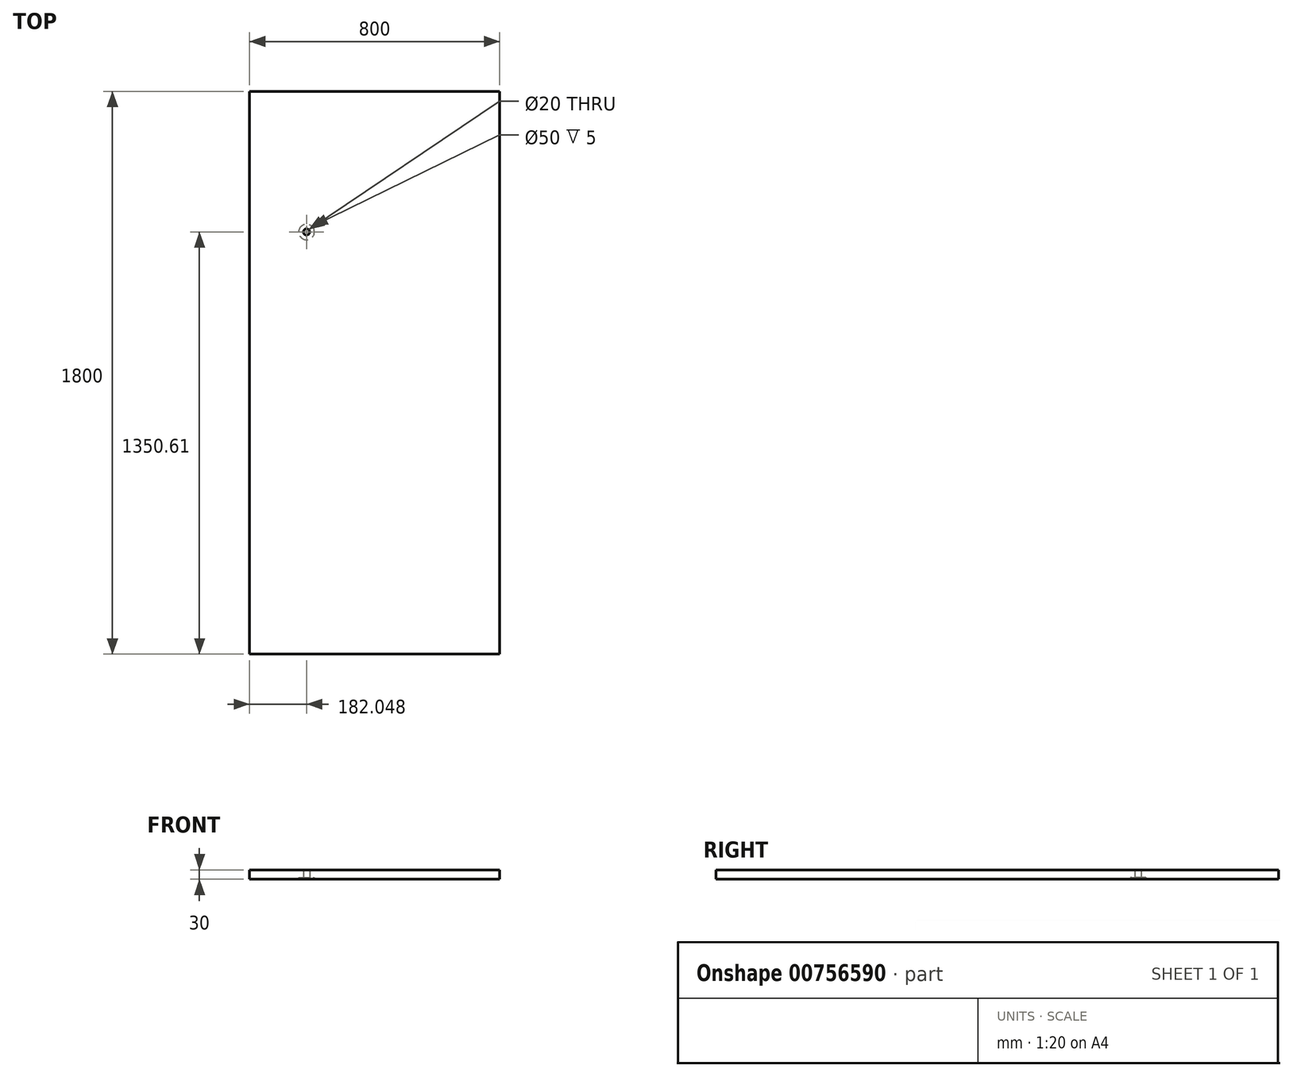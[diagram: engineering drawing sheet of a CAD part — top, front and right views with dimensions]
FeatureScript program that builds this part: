
annotation { "Feature Type Name" : "Feature", "Feature Type Description" : "" }
export const myFeature = defineFeature(function(context is Context, id is Id, definition is map)
    precondition{}
    {
        {
            var Q0;
            Q0=qCreatedBy(makeId("Top.planeOp"),FACE);
            var sketch = newSketch(context, id + "F0", { "sketchPlane" : qUnion([Q0])});
            skLineSegment(sketch, "E0.bottom", {"start": v(-400, 900) * mm, "end": v(400, 900) * mm});
            skLineSegment(sketch, "E0.top", {"start": v(-400, -900) * mm, "end": v(400, -900) * mm});
            skLineSegment(sketch, "E0.left", {"start": v(-400, 900) * mm, "end": v(-400, -900) * mm});
            skLineSegment(sketch, "E0.right", {"start": v(400, 900) * mm, "end": v(400, -900) * mm});
            skPoint(sketch, "E0.middle", {"position": v(0, 0) * mm});
            skSolve(sketch);
        }
        {
            var Q0;
            Q0 = qSketchRegion(id + "F0", true);
            extrude(context, id + "F1", {"entities" : qUnion([Q0]), "depth" : 30 * mm, "offsetDistance" : 25 * mm});
        }
        {
            var Q0;
            Q0=qCreatedBy(makeId("Top.planeOp"),FACE);
            var sketch = newSketch(context, id + "F2", { "sketchPlane" : qUnion([Q0])});
            skCircle(sketch, "E1", {"center": v(-217.95, 450.61) * mm, "radius": 116.6 * mm});
            skSolve(sketch);
        }
        {
            var Q0;
            Q0=sQuery(id+"F2.wireOp",VERTEX,"E1.center");
            var Q1;
            Q1=makeQuery(id+"F1.opExtrude","SWEPT_BODY",BODY,{"disambiguationData":[OSD([sQuery(id+"F0.wireOp",EDGE,"E0.bottom"),sQuery(id+"F0.wireOp",EDGE,"E0.top"),sQuery(id+"F0.wireOp",EDGE,"E0.left"),sQuery(id+"F0.wireOp",EDGE,"E0.right")])]});
            hole(context, id + "F3", {"style" : HoleStyle.C_BORE, "endStyle" : HoleEndStyle.THROUGH, "oppositeDirection" : true, "holeDiameter" : 20 * mm, "cBoreDiameter" : 50 * mm, "cBoreDepth" : 5 * mm, "majorDiameter" : 5 * mm, "isTappedThrough" : true, "tappedDepth" : 12 * mm, "tapClearance" : 3, "startFromSketch" : true, "locations" : qUnion([Q0]), "scope" : qUnion([Q1])});
        }
    });
